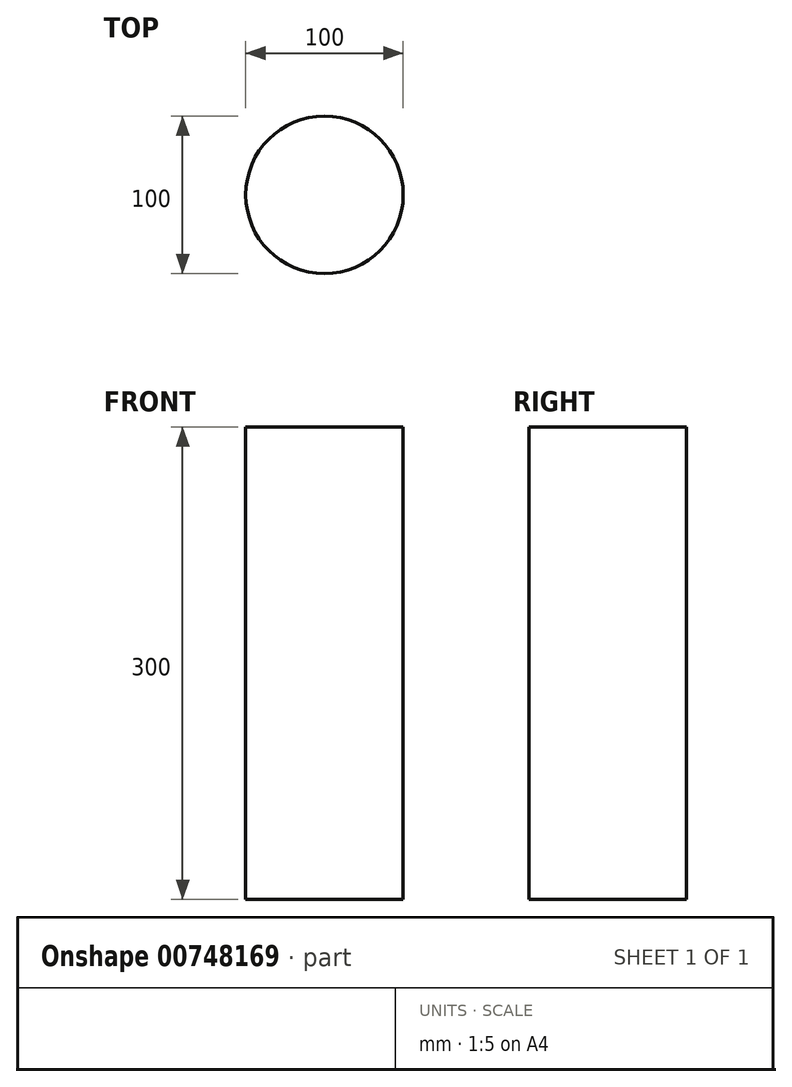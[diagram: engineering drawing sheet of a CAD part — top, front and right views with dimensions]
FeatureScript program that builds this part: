
annotation { "Feature Type Name" : "Feature", "Feature Type Description" : "" }
export const myFeature = defineFeature(function(context is Context, id is Id, definition is map)
    precondition{}
    {
        {
            var Q0;
            Q0=qCreatedBy(makeId("Top.planeOp"),FACE);
            var sketch = newSketch(context, id + "F0", { "sketchPlane" : qUnion([Q0])});
            skCircle(sketch, "E0", {"center": v(0, 1.27) * mm, "radius": 50 * mm});
            skSolve(sketch);
        }
        {
            var Q0;
            Q0 = qSketchRegion(id + "F0", true);
            extrude(context, id + "F1", {"entities" : qUnion([Q0]), "depth" : 300 * mm, "offsetDistance" : 25 * mm});
        }
    });
